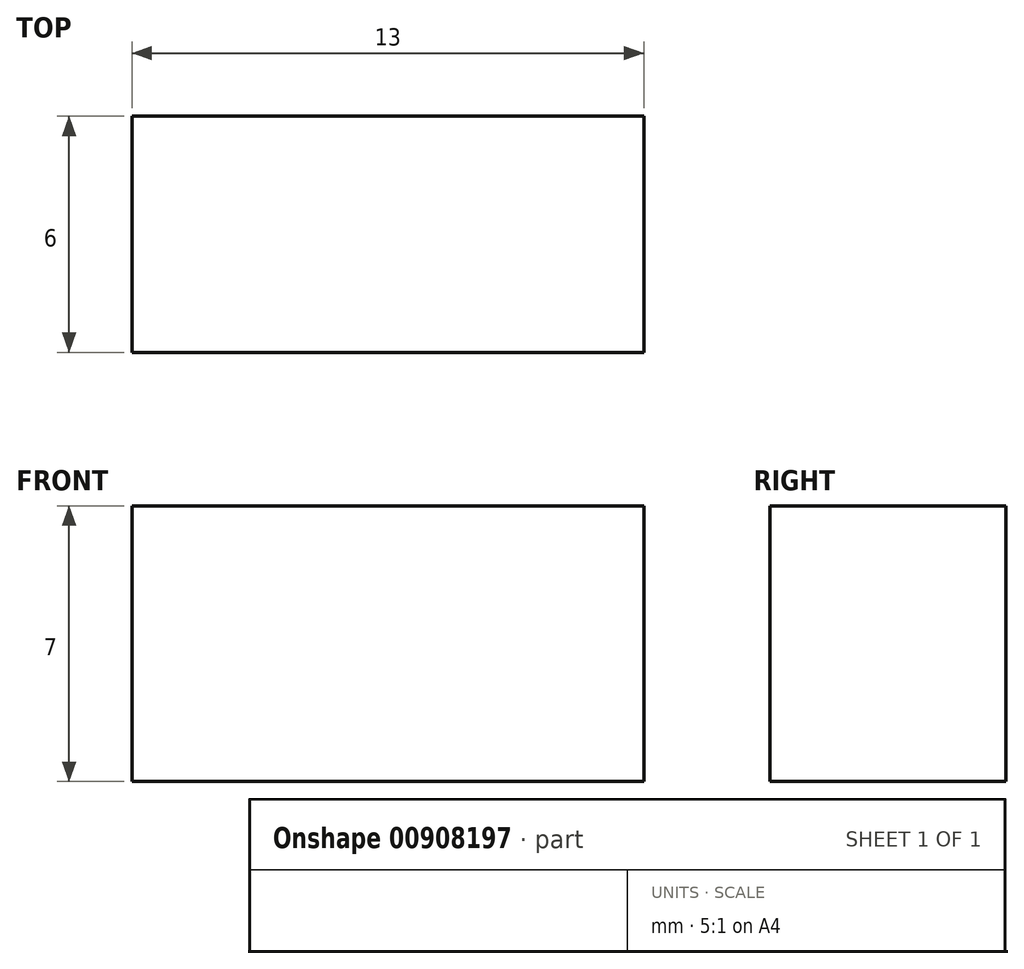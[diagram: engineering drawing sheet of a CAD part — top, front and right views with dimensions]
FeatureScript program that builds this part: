
annotation { "Feature Type Name" : "Feature", "Feature Type Description" : "" }
export const myFeature = defineFeature(function(context is Context, id is Id, definition is map)
    precondition{}
    {
        {
            var Q0;
            Q0=qCreatedBy(makeId("Top.planeOp"),FACE);
            var sketch = newSketch(context, id + "F0", { "sketchPlane" : qUnion([Q0])});
            skLineSegment(sketch, "E0.bottom", {"start": v(6.5, -3) * mm, "end": v(-6.5, -3) * mm});
            skLineSegment(sketch, "E0.top", {"start": v(6.5, 3) * mm, "end": v(-6.5, 3) * mm});
            skLineSegment(sketch, "E0.left", {"start": v(6.5, -3) * mm, "end": v(6.5, 3) * mm});
            skLineSegment(sketch, "E0.right", {"start": v(-6.5, -3) * mm, "end": v(-6.5, 3) * mm});
            skPoint(sketch, "E0.middle", {"position": v(0, 0) * mm});
            skSolve(sketch);
        }
        {
            var Q0;
            Q0 = qSketchRegion(id + "F0", true);
            extrude(context, id + "F1", {"entities" : qUnion([Q0]), "depth" : 7 * mm, "offsetDistance" : 25 * mm});
        }
    });
